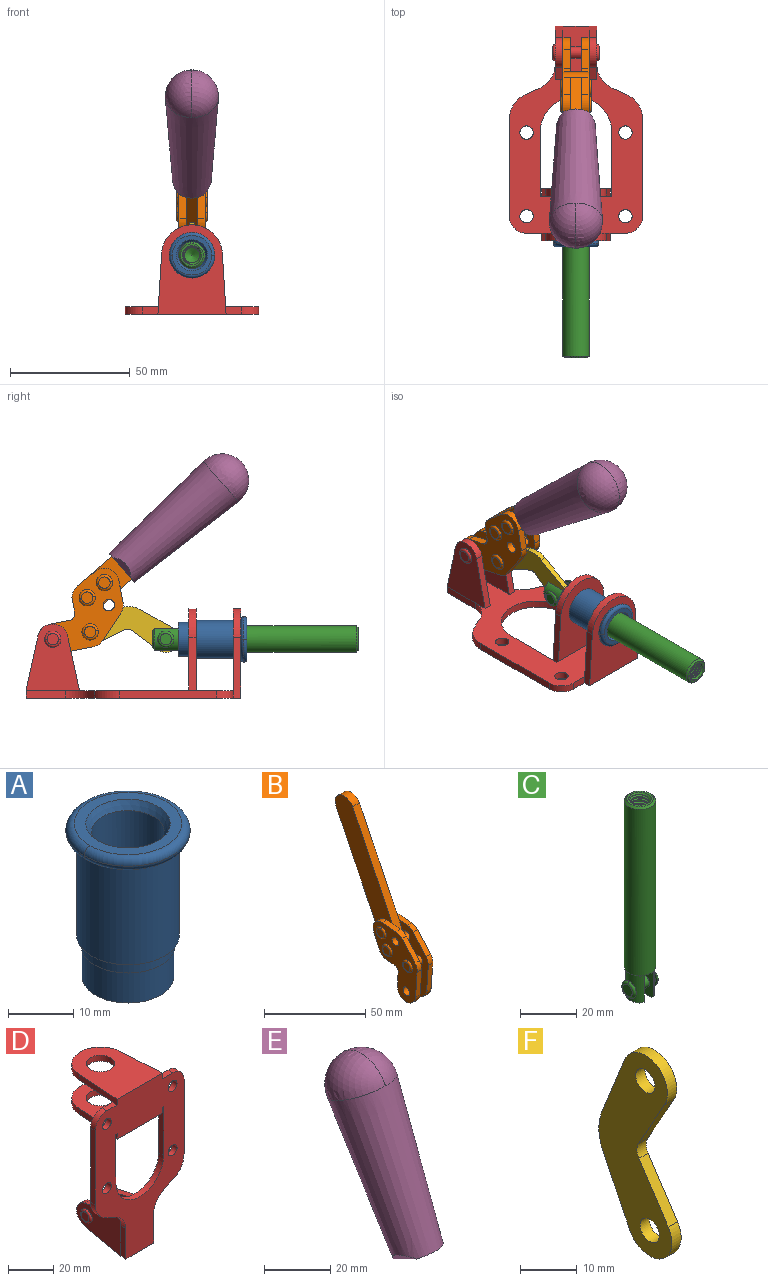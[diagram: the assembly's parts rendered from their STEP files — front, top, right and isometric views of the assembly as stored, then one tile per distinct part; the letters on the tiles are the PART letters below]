
ASSEMBLY  parts=6 mates=6
PART A: 15 faces, bbox 20.6x20.6x28.7 mm
  f0: torus R=8.26mm, axis (0,0,1), area 56.8mm2, adj f1,f10,f12
  f1: torus R=8.26mm, axis (0,0,1), area 56.8mm2, adj f0,f6,f13
  f2: cylinder r=5.59mm len=25.91mm, axis (0,0,1), area 909.6mm2, adj f3,f4
  f3: cone r=6.86mm half-angle=45deg, axis (0,0,-1), area 70.2mm2, adj f2,f14
  f4: cone r=6.47mm half-angle=30deg, axis (0,0,1), area 66.7mm2, adj f2,f13
  f5: cylinder r=7.04mm len=14.07mm, axis (0,0,1), area 252.6mm2, adj f11,f14
  f6: torus R=8.26mm, axis (0,0,1), area 56.8mm2, adj f1,f12,f13
  f7: cylinder r=7.16mm len=14.33mm, axis (0,0,1), area 91.5mm2, adj f9,f11
  f8: cylinder r=7.86mm len=18.42mm, axis (0,0,1), area 909.6mm2, adj f9,f10
  f9: plane 15.72x15.72mm, normal (0,0,-1), area 33mm2, adj f7,f8
  f10: plane 16.51x16.51mm, normal (0,0,-1), area 19.9mm2, adj f0,f8,f12
  f11: plane 14.33x14.33mm, normal (0,0,-1), area 5.7mm2, adj f5,f7
  f12: torus R=8.26mm, axis (0,0,1), area 56.8mm2, adj f0,f6,f10
  f13: plane 16.51x16.51mm, normal (0,0,1), area 82.7mm2, adj f1,f4,f6
  f14: plane 14.07x14.07mm, normal (0,0,-1), area 7.8mm2, adj f3,f5
PART B: 59 faces, bbox 12.9x60.2x99.6 mm
  f0: torus R=2.39mm, axis (-1,0,0), area 14.9mm2, adj f20,f43,f51
  f1: torus R=2.39mm, axis (-1,0,0), area 14.9mm2, adj f19,f42,f51
  f2: torus R=2.39mm, axis (-1,0,0), area 14.9mm2, adj f18,f35,f51
  f3: torus R=2.39mm, axis (-1,0,0), area 14.9mm2, adj f14,f17,f23
  f4: torus R=2.39mm, axis (-1,0,0), area 14.9mm2, adj f13,f16,f23
  f5: torus R=2.39mm, axis (-1,0,0), area 14.9mm2, adj f12,f15,f23
  f6: cylinder r=2.39mm len=4.78mm, axis (1,0,0), area 46.5mm2, adj f48,f50,f51
  f7: cylinder r=2.39mm len=4.78mm, axis (1,0,0), area 46.5mm2, adj f50,f51
  f8: cylinder r=6.35mm len=12.68mm, axis (1,0,0), area 61.8mm2, adj f38,f39,f50,f51
  f9: cylinder r=2.39mm len=4.78mm, axis (-1,0,0), area 70.5mm2, adj f46,f50
  f10: cylinder r=2.39mm len=4.78mm, axis (-1,0,0), area 46.5mm2, adj f23,f45,f46
  f11: cylinder r=2.39mm len=4.78mm, axis (-1,0,0), area 46.5mm2, adj f23,f46
  f12: plane 4.78x4.78mm, normal (1,0,0), area 17.9mm2, adj f5,f15
  f13: plane 4.78x4.78mm, normal (1,0,0), area 17.9mm2, adj f4,f16
  f14: plane 4.78x4.78mm, normal (1,0,0), area 17.9mm2, adj f3,f17
  f15: torus R=2.39mm, axis (-1,0,0), area 14.9mm2, adj f5,f12,f23
  f16: torus R=2.39mm, axis (-1,0,0), area 14.9mm2, adj f4,f13,f23
  f17: torus R=2.39mm, axis (-1,0,0), area 14.9mm2, adj f3,f14,f23
  f18: plane 4.78x4.78mm, normal (-1,0,0), area 17.9mm2, adj f2,f35
  f19: plane 4.78x4.78mm, normal (-1,0,0), area 17.9mm2, adj f1,f42
  f20: plane 4.78x4.78mm, normal (-1,0,0), area 17.9mm2, adj f0,f43
  f21: plane 2.26x0.2mm, normal (1,0,0), area 0.2mm2, adj f31,f44
  f22: plane 2.26x0.2mm, normal (-1,0,0), area 0.2mm2, adj f41,f44
  f23: plane 39.37x30.77mm, normal (1,0,0), area 565.5mm2, adj f3,f4,f5,f10,f11,f15,f16,f17
  f24: cylinder r=6.1mm len=4.15mm, axis (-1,0,0), area 14.7mm2, adj f23,f25,f32,f46
  f25: plane 10.25x9.01mm, normal (0,-0.75,0.66), area 42.3mm2, adj f23,f24,f26,f46
  f26: cylinder r=6.35mm len=4.64mm, axis (-1,0,0), area 15.6mm2, adj f23,f25,f27,f46
  f27: plane 15.84x3.1mm, normal (0,-1,-0.07), area 49.2mm2, adj f23,f26,f28,f46
  f28: cylinder r=6.35mm len=12.68mm, axis (-1,0,0), area 61.8mm2, adj f23,f27,f29,f46
  f29: plane 8.11x3.1mm, normal (0,1,0.07), area 25.2mm2, adj f23,f28,f30,f46
  f30: cylinder r=3.05mm len=3.25mm, axis (-1,0,0), area 14.8mm2, adj f23,f29,f31,f46
  f31: plane 5.99x3.1mm, normal (0,0.07,-1), area 18.6mm2, adj f21,f23,f30,f44,f46
  f32: plane 9.5x3.1mm, normal (0,-0.07,1), area 29.5mm2, adj f23,f24,f33,f46,f47
  f33: cylinder r=6.1mm len=8.63mm, axis (-1,0,0), area 39.1mm2, adj f23,f32,f34,f47
  f34: plane 8.65x3.96mm, normal (0,0.91,-0.42), area 29.5mm2, adj f23,f33,f44,f47
  f35: torus R=2.39mm, axis (-1,0,0), area 14.9mm2, adj f2,f18,f51
  f36: plane 10.25x9.01mm, normal (0,-0.75,0.66), area 42.3mm2, adj f37,f49,f50,f51
  f37: cylinder r=6.35mm len=4.64mm, axis (1,0,0), area 15.6mm2, adj f36,f38,f50,f51
  f38: plane 15.84x3.1mm, normal (0,-1,-0.07), area 49.2mm2, adj f8,f37,f50,f51
  f39: plane 8.11x3.1mm, normal (0,1,0.07), area 25.2mm2, adj f8,f40,f50,f51
  f40: cylinder r=3.05mm len=3.25mm, axis (1,0,0), area 14.8mm2, adj f39,f41,f50,f51
  f41: plane 5.99x3.1mm, normal (0,0.07,-1), area 18.6mm2, adj f22,f40,f44,f50,f51
  f42: torus R=2.39mm, axis (-1,0,0), area 14.9mm2, adj f1,f19,f51
  f43: torus R=2.39mm, axis (-1,0,0), area 14.9mm2, adj f0,f20,f51
  f44: cylinder r=6.35mm len=12.12mm, axis (-1,0,0), area 128.9mm2, adj f21,f22,f23,f31,f34,f41,f46,f47
  f45: plane 2.65x1.35mm, normal (1,0,0), area 1mm2, adj f10,f55
  f46: plane 39.08x20.42mm, normal (-1,0,0), area 412.5mm2, adj f9,f10,f11,f24,f25,f26,f27,f28
  f47: plane 77.62x39.82mm, normal (1,0,0), area 850mm2, adj f32,f33,f34,f44,f53,f54,f55
  f48: plane 2.65x1.35mm, normal (-1,0,0), area 1mm2, adj f6,f55
  f49: cylinder r=6.1mm len=4.15mm, axis (1,0,0), area 14.7mm2, adj f36,f50,f51,f56
  f50: plane 39.08x20.42mm, normal (1,0,0), area 412.5mm2, adj f6,f7,f8,f9,f36,f37,f38,f39
  f51: plane 39.37x30.77mm, normal (-1,0,0), area 565.5mm2, adj f0,f1,f2,f6,f7,f8,f35,f36
  f52: plane 8.65x3.96mm, normal (0,0.91,-0.42), area 29.5mm2, adj f44,f51,f57,f58
  f53: plane 68.49x33.4mm, normal (0,0.9,-0.44), area 358.1mm2, adj f44,f47,f54,f58
  f54: cylinder r=6.35mm len=12.06mm, axis (1,0,0), area 93.7mm2, adj f47,f53,f55,f58
  f55: plane 68.49x33.4mm, normal (0,-0.9,0.44), area 358.1mm2, adj f44,f45,f46,f47,f48,f50,f54,f58
  f56: plane 9.5x3.1mm, normal (0,-0.07,1), area 29.5mm2, adj f49,f50,f51,f57,f58
  f57: cylinder r=6.1mm len=8.63mm, axis (1,0,0), area 39.1mm2, adj f51,f52,f56,f58
  f58: plane 77.62x39.82mm, normal (-1,0,0), area 850mm2, adj f44,f52,f53,f54,f55,f56,f57
PART C: 48 faces, bbox 12.6x11.1x86.1 mm
  f0: torus R=2.41mm, axis (-1,0,0), area 15mm2, adj f30,f32,f34
  f1: torus R=2.41mm, axis (-1,0,0), area 15mm2, adj f29,f31,f33
  f2: cylinder r=5.54mm len=72.39mm, axis (0,0,1), area 2518.5mm2, adj f3,f4,f42,f43
  f3: cone r=5.54mm half-angle=45deg, axis (0,0,1), area 7.6mm2, adj f2,f5,f41
  f4: cone r=5.54mm half-angle=45deg, axis (0,0,-1), area 34.9mm2, adj f2,f39
  f5: cylinder r=5.08mm len=11.48mm, axis (0,0,1), area 108.3mm2, adj f3,f7,f8,f41
  f6: cylinder r=2.41mm len=4.83mm, axis (-1,0,0), area 71.2mm2, adj f40,f41
  f7: cylinder r=2.41mm len=4.83mm, axis (-1,0,0), area 7.6mm2, adj f5,f34
  f8: cone r=5.08mm half-angle=45deg, axis (0,0,1), area 10.6mm2, adj f5,f37,f41
  f9: cone r=3.98mm half-angle=45deg, axis (0,0,1), area 17.6mm2, adj f27,f39,f45,f46,f47
  f10: cylinder r=2.41mm len=4.83mm, axis (-1,0,0), area 7.6mm2, adj f33,f38
  f11: cylinder r=3.2mm len=6.4mm, axis (0,0,1), area 78.4mm2, adj f12,f28,f44,f45,f47
  f12: cylinder r=3.2mm len=6.4mm, axis (0,0,1), area 10.5mm2, adj f11,f13,f45,f47
  f13: cylinder r=3.2mm len=6.4mm, axis (0,0,1), area 10.5mm2, adj f12,f14,f45,f47
  f14: cylinder r=3.2mm len=6.4mm, axis (0,0,1), area 10.5mm2, adj f13,f15,f45,f47
  f15: cylinder r=3.2mm len=6.4mm, axis (0,0,1), area 10.5mm2, adj f14,f16,f45,f47
  f16: cylinder r=3.2mm len=6.4mm, axis (0,0,1), area 10.5mm2, adj f15,f17,f45,f47
  f17: cylinder r=3.2mm len=6.4mm, axis (0,0,1), area 10.5mm2, adj f16,f18,f45,f47
  f18: cylinder r=3.2mm len=6.4mm, axis (0,0,1), area 10.5mm2, adj f17,f19,f45,f47
  f19: cylinder r=3.2mm len=6.4mm, axis (0,0,1), area 10.5mm2, adj f18,f20,f45,f47
  f20: cylinder r=3.2mm len=6.4mm, axis (0,0,1), area 10.5mm2, adj f19,f21,f45,f47
  f21: cylinder r=3.2mm len=6.4mm, axis (0,0,1), area 10.5mm2, adj f20,f22,f45,f47
  f22: cylinder r=3.2mm len=6.4mm, axis (0,0,1), area 10.5mm2, adj f21,f23,f45,f47
  f23: cylinder r=3.2mm len=6.4mm, axis (0,0,1), area 10.5mm2, adj f22,f24,f45,f47
  f24: cylinder r=3.2mm len=6.4mm, axis (0,0,1), area 10.5mm2, adj f23,f25,f45,f47
  f25: cylinder r=3.2mm len=6.4mm, axis (0,0,1), area 10.5mm2, adj f24,f26,f45,f47
  f26: cylinder r=3.2mm len=6.4mm, axis (0,0,1), area 10.5mm2, adj f25,f27,f45,f47
  f27: cylinder r=3.2mm len=6.4mm, axis (0,0,1), area 7.4mm2, adj f9,f26,f45,f47
  f28: cone r=3.2mm half-angle=60deg, axis (0,0,1), area 37.2mm2, adj f11
  f29: plane 4.83x4.83mm, normal (-1,0,0), area 18.3mm2, adj f1,f31
  f30: plane 4.83x4.83mm, normal (1,0,0), area 18.3mm2, adj f0,f32
  f31: torus R=2.41mm, axis (-1,0,0), area 15mm2, adj f1,f29,f33
  f32: torus R=2.41mm, axis (-1,0,0), area 15mm2, adj f0,f30,f34
  f33: plane 6.83x6.83mm, normal (1,0,0), area 18.3mm2, adj f1,f10,f31
  f34: plane 6.83x6.83mm, normal (-1,0,0), area 18.3mm2, adj f0,f7,f32
  f35: cone r=5.08mm half-angle=45deg, axis (0,0,1), area 10.6mm2, adj f36,f38,f40
  f36: plane 7.25x1.97mm, normal (0,0,-1), area 10mm2, adj f35,f40
  f37: plane 7.25x1.97mm, normal (0,0,-1), area 10mm2, adj f8,f41
  f38: cylinder r=5.08mm len=11.48mm, axis (0,0,1), area 108.3mm2, adj f10,f35,f40,f42
  f39: plane 9.55x9.55mm, normal (0,0,1), area 22mm2, adj f4,f9
  f40: plane 12.76x10.09mm, normal (1,0,0), area 95.7mm2, adj f6,f35,f36,f38,f42,f43
  f41: plane 12.76x10.09mm, normal (-1,0,0), area 95.7mm2, adj f3,f5,f6,f8,f37,f43
  f42: cone r=5.54mm half-angle=45deg, axis (0,0,1), area 7.6mm2, adj f2,f38,f40
  f43: plane 11.07x4.7mm, normal (0,0,-1), area 50.4mm2, adj f2,f40,f41
  f44: plane 0.89x0.62mm, normal (-1,0,0), area 0.3mm2, adj f11,f45,f46,f47
  f45: bspline ~24.8x7.63mm, area 266.6mm2, adj f9,f11,f12,f13,f14,f15,f16,f17
  f46: bspline ~24.87x7.63mm, area 73.6mm2, adj f9,f44,f45,f47
  f47: bspline ~24.98x7.63mm, area 272.5mm2, adj f9,f11,f12,f13,f14,f15,f16,f17
PART D: 55 faces, bbox 55.7x37.4x89.8 mm
  f0: torus R=2.41mm, axis (-1,0,0), area 15mm2, adj f11,f15,f25
  f1: torus R=2.41mm, axis (-1,0,0), area 15mm2, adj f10,f12,f22
  f2: cylinder r=2.78mm len=5.56mm, axis (0,-1,0), area 54.2mm2, adj f30,f54
  f3: cylinder r=14.99mm len=29.97mm, axis (0,-1,0), area 145.9mm2, adj f30,f49,f53,f54
  f4: cylinder r=2.78mm len=5.56mm, axis (0,-1,0), area 54.2mm2, adj f30,f54
  f5: cylinder r=2.78mm len=5.56mm, axis (0,-1,0), area 54.2mm2, adj f30,f54
  f6: cylinder r=2.78mm len=5.56mm, axis (0,-1,0), area 54.2mm2, adj f30,f54
  f7: cylinder r=6.35mm len=12.7mm, axis (0,0,1), area 123.6mm2, adj f27,f51
  f8: cylinder r=6.35mm len=12.7mm, axis (0,0,-1), area 124.7mm2, adj f21,f35
  f9: cylinder r=2.41mm len=11.18mm, axis (-1,0,0), area 169.4mm2, adj f16,f19
  f10: plane 4.83x4.83mm, normal (1,0,0), area 18.3mm2, adj f1,f12
  f11: plane 4.83x4.83mm, normal (-1,0,0), area 18.3mm2, adj f0,f15
  f12: torus R=2.41mm, axis (-1,0,0), area 15mm2, adj f1,f10,f22
  f13: cylinder r=6.35mm len=12.41mm, axis (1,0,0), area 53.4mm2, adj f18,f19,f22,f23
  f14: cylinder r=6.35mm len=12.41mm, axis (-1,0,0), area 53.4mm2, adj f16,f17,f24,f25
  f15: torus R=2.41mm, axis (-1,0,0), area 15mm2, adj f0,f11,f25
  f16: plane 27.86x22.35mm, normal (1,0,0), area 425.4mm2, adj f9,f14,f17,f24,f30
  f17: plane 22.86x4.97mm, normal (0,0.21,0.98), area 72.5mm2, adj f14,f16,f25,f30
  f18: plane 22.86x4.97mm, normal (0,0.21,0.98), area 72.5mm2, adj f13,f19,f22,f30
  f19: plane 27.86x22.35mm, normal (-1,0,0), area 425.4mm2, adj f9,f13,f18,f23,f30
  f20: cylinder r=12.7mm len=25.35mm, axis (0,0,-1), area 119.8mm2, adj f21,f34,f35,f36
  f21: plane 34.21x28.07mm, normal (0,0,-1), area 702.4mm2, adj f8,f20,f30,f34,f36
  f22: plane 27.96x22.45mm, normal (1,0,0), area 407.2mm2, adj f1,f12,f13,f18,f23,f30,f42,f43
  f23: plane 22.86x4.97mm, normal (0,0.21,-0.98), area 72.5mm2, adj f13,f19,f22,f44
  f24: plane 22.86x4.97mm, normal (0,0.21,-0.98), area 72.5mm2, adj f14,f16,f25,f44
  f25: plane 27.86x22.35mm, normal (-1,0,0), area 407.1mm2, adj f0,f14,f15,f17,f24,f30,f45,f46
  f26: plane 3.1x0.95mm, normal (0,0,-1), area 2.7mm2, adj f30,f49,f50,f54
  f27: plane 34.21x28.07mm, normal (0,0,1), area 702.4mm2, adj f7,f28,f30,f50,f52
  f28: cylinder r=12.7mm len=25.35mm, axis (0,0,1), area 118.8mm2, adj f27,f50,f51,f52
  f29: plane 3.1x0.95mm, normal (0,0,-1), area 2.7mm2, adj f30,f52,f53,f54
  f30: plane 86.54x55.63mm, normal (0,1,0), area 2362.9mm2, adj f2,f3,f4,f5,f6,f16,f17,f18
  f31: plane 40.56x3.1mm, normal (-1,0,0), area 125.7mm2, adj f30,f32,f48,f54
  f32: cylinder r=7.11mm len=7.11mm, axis (0,-1,0), area 34.6mm2, adj f30,f31,f33,f54
  f33: plane 6.67x3.1mm, normal (0,0,1), area 20.4mm2, adj f30,f32,f34,f54
  f34: plane 25.39x3.13mm, normal (-1,0.06,0), area 79.5mm2, adj f20,f21,f33,f35,f54
  f35: plane 37.31x28.45mm, normal (0,0,1), area 789.9mm2, adj f8,f20,f34,f36,f54
  f36: plane 25.39x3.13mm, normal (1,0.06,0), area 79.5mm2, adj f20,f21,f35,f37,f54
  f37: plane 6.67x3.1mm, normal (0,0,1), area 20.4mm2, adj f30,f36,f38,f54
  f38: cylinder r=7.11mm len=7.11mm, axis (0,-1,0), area 34.6mm2, adj f30,f37,f39,f54
  f39: plane 40.56x3.1mm, normal (1,0,0), area 125.7mm2, adj f30,f38,f40,f54
  f40: cylinder r=11.18mm len=10.16mm, axis (0,-1,0), area 39.5mm2, adj f30,f39,f41,f54
  f41: plane 6.09x3.1mm, normal (0.42,0,-0.91), area 20.8mm2, adj f30,f40,f42,f54
  f42: cylinder r=11.18mm len=9.41mm, axis (0,-1,0), area 37.2mm2, adj f22,f30,f41,f43,f54
  f43: plane 16.5x3.1mm, normal (1,0,0), area 51.1mm2, adj f22,f42,f44,f54
  f44: plane 17.37x3.1mm, normal (0,0,-1), area 53.8mm2, adj f23,f24,f30,f43,f45,f54
  f45: plane 16.5x3.1mm, normal (-1,0,0), area 51.1mm2, adj f25,f44,f46,f54
  f46: cylinder r=11.18mm len=9.41mm, axis (0,-1,0), area 37.2mm2, adj f25,f30,f45,f47,f54
  f47: plane 6.09x3.1mm, normal (-0.42,0,-0.91), area 20.8mm2, adj f30,f46,f48,f54
  f48: cylinder r=11.18mm len=10.16mm, axis (0,-1,0), area 39.5mm2, adj f30,f31,f47,f54
  f49: plane 26.54x3.1mm, normal (-1,0,0), area 82.3mm2, adj f3,f26,f30,f54
  f50: plane 25.39x3.1mm, normal (1,0.06,0), area 78.8mm2, adj f26,f27,f28,f51,f54
  f51: plane 37.31x28.45mm, normal (0,0,-1), area 789.9mm2, adj f7,f28,f50,f52,f54
  f52: plane 25.39x3.1mm, normal (-1,0.06,0), area 78.8mm2, adj f27,f28,f29,f51,f54
  f53: plane 26.54x3.1mm, normal (1,0,0), area 82.3mm2, adj f3,f29,f30,f54
  f54: plane 89.66x55.63mm, normal (0,-1,0), area 2678.5mm2, adj f2,f3,f4,f5,f6,f26,f29,f31
PART E: 11 faces, bbox 22.3x42.6x64.5 mm
  f0: sphere r=11.13mm, area 411.4mm2, adj f1,f8
  f1: cone r=11.11mm half-angle=3.3deg, axis (0,0.44,0.9), area 3251.8mm2, adj f0,f7,f8,f9,f10
  f2: cylinder r=6.16mm len=11.7mm, axis (1,0,0), area 89.5mm2, adj f3,f4,f5,f6
  f3: plane 60.23x36.75mm, normal (-1,0,0), area 763.6mm2, adj f2,f4,f6,f10
  f4: plane 51.37x25.05mm, normal (0,0.9,-0.44), area 264.2mm2, adj f2,f3,f5,f10
  f5: plane 60.23x36.75mm, normal (1,0,0), area 763.6mm2, adj f2,f4,f6,f10
  f6: plane 51.37x25.05mm, normal (0,-0.9,0.44), area 264.2mm2, adj f2,f3,f5,f10
  f7: plane 9.95x5.95mm, normal (0.71,-0.31,-0.64), area 25.8mm2, adj f1,f10
  f8: sphere r=11.13mm, area 411.4mm2, adj f0,f1
  f9: plane 9.95x5.95mm, normal (-0.71,-0.31,-0.64), area 25.8mm2, adj f1,f10
  f10: plane 14.27x11.38mm, normal (0,-0.44,-0.9), area 106.7mm2, adj f1,f3,f4,f5,f6,f7,f9
PART F: 12 faces, bbox 2.3x18.2x42.8 mm
  f0: cylinder r=2.4mm len=4.8mm, axis (1,0,0), area 34.9mm2, adj f4,f11
  f1: cylinder r=10.41mm len=8.47mm, axis (1,0,0), area 20.2mm2, adj f4,f9,f10,f11
  f2: cylinder r=3.05mm len=3.16mm, axis (1,0,0), area 7.7mm2, adj f4,f6,f7,f11
  f3: cylinder r=2.4mm len=4.8mm, axis (1,0,0), area 34.9mm2, adj f4,f11
  f4: plane 42.81x18.23mm, normal (-1,0,0), area 414.1mm2, adj f0,f1,f2,f3,f5,f6,f7,f8
  f5: cylinder r=5.54mm len=10.67mm, axis (1,0,0), area 41.8mm2, adj f4,f6,f10,f11
  f6: plane 11.66x6.53mm, normal (0,-0.87,-0.49), area 30.9mm2, adj f2,f4,f5,f11
  f7: plane 11.17x7.33mm, normal (0,-0.84,0.55), area 30.9mm2, adj f2,f4,f8,f11
  f8: cylinder r=5.54mm len=10.51mm, axis (1,0,0), area 41.8mm2, adj f4,f7,f9,f11
  f9: plane 13.67x6.67mm, normal (0,0.9,-0.44), area 35.1mm2, adj f1,f4,f8,f11
  f10: plane 14.1x5.7mm, normal (0,0.93,0.37), area 35.1mm2, adj f1,f4,f5,f11
  f11: plane 42.81x18.23mm, normal (1,0,0), area 414.1mm2, adj f0,f1,f2,f3,f5,f6,f7,f8
PLACE A rot(axis=(1,0,0),90deg) t=(0,9.14,0)mm
PLACE B rot(axis=(1,0,0),75deg) t=(0,3.86,9.14)mm
PLACE C rot(axis=(1,0,0),90deg) t=(0,9.52,0)mm
PLACE D rot(axis=(1,0,0),90deg) t=(0,9.14,0)mm fixed
PLACE E rot(axis=(1,0,0),75deg) t=(-0.04,3.86,9.14)mm
PLACE F rot(axis=(1,0,0),97.5deg) t=(0,12.59,2.22)mm
MATE slider C.f2 <-> D.f7  axis (0,-1,0) through (0,-49.26,24.61)mm
MATE revolute F.f5 <-> C.f6  axis (1,0,0) through (0,-5.96,24.61)mm
MATE revolute F.f3 <-> B.f4  axis (1,0,0) through (0,25.65,27.64)mm
MATE revolute D.f0 <-> B.f7  axis (-1,0,0) through (0,41.23,24.61)mm
MATE fastened E.f2 <-> B.f54  axis (1,0,0) through (-2.35,-30.66,91.94)mm
MATE fastened A.f0 <-> D.f7  axis (0,1,0) through (0,-37.25,24.61)mm
